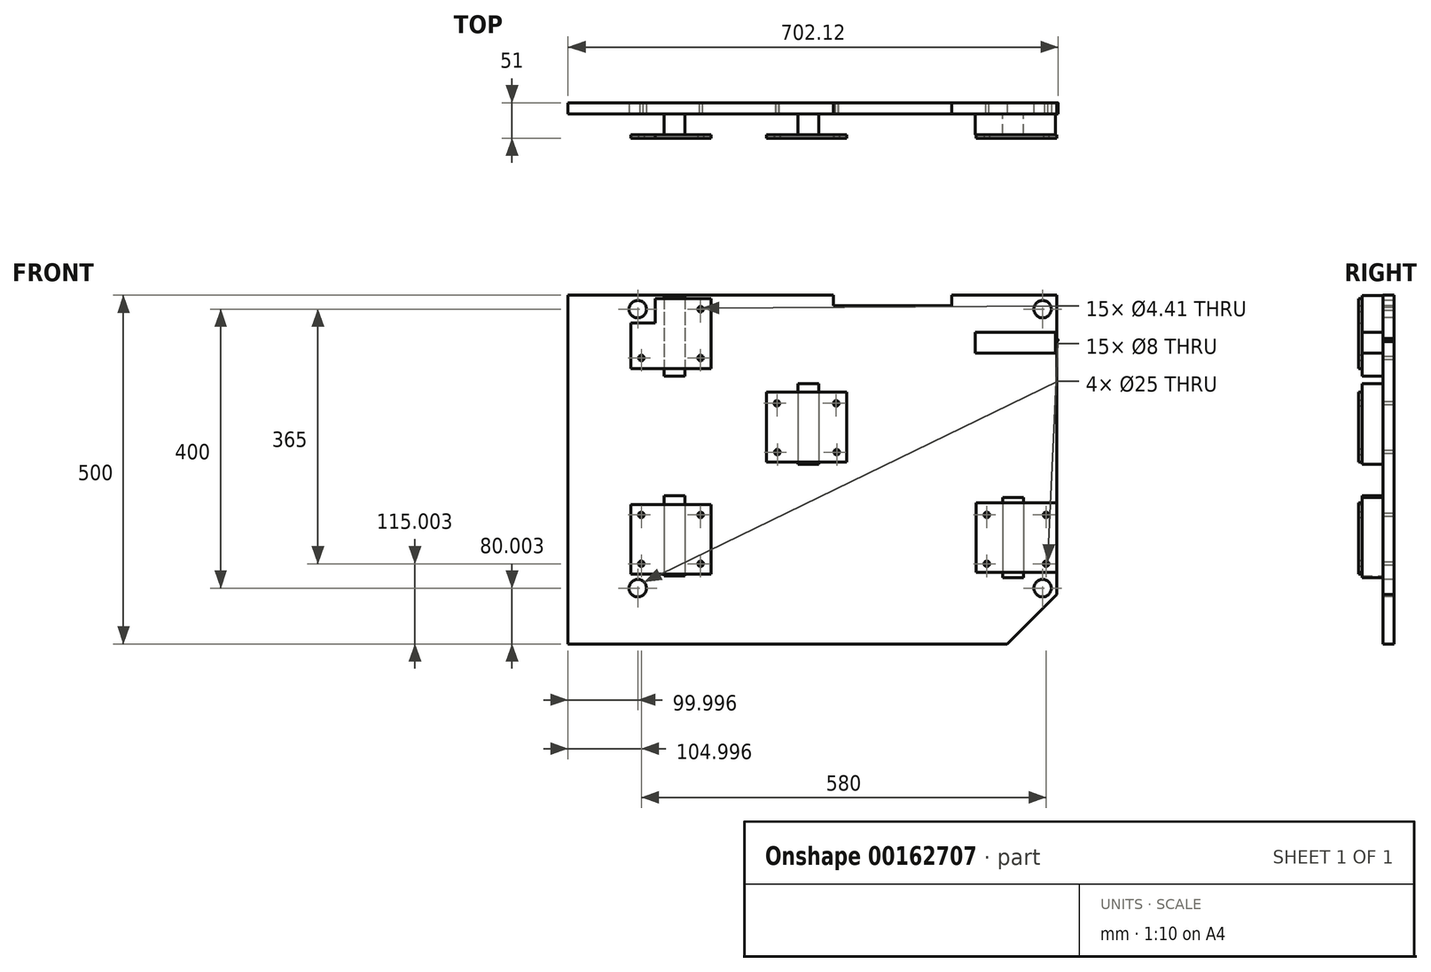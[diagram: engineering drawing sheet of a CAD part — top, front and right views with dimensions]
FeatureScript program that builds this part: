
annotation { "Feature Type Name" : "Feature", "Feature Type Description" : "" }
export const myFeature = defineFeature(function(context is Context, id is Id, definition is map)
    precondition{}
    {
        {
            var Q0;
            Q0=qCreatedBy(makeId("Front.planeOp"),FACE);
            var sketch = newSketch(context, id + "F0", { "sketchPlane" : qUnion([Q0])});
            skLineSegment(sketch, "E0", {"start": v(-699.91, -435.58) * mm, "end": v(-699.91, 64.42) * mm});
            skLineSegment(sketch, "E1", {"start": v(-699.91, 64.42) * mm, "end": v(-319.91, 64.42) * mm});
            skLineSegment(sketch, "E2", {"start": v(-319.91, 64.42) * mm, "end": v(-319.91, 49.42) * mm});
            skLineSegment(sketch, "E3", {"start": v(-319.91, 49.42) * mm, "end": v(-149.91, 49.42) * mm});
            skLineSegment(sketch, "E4", {"start": v(-149.91, 49.42) * mm, "end": v(-149.91, 64.42) * mm});
            skLineSegment(sketch, "E5", {"start": v(-149.91, 64.42) * mm, "end": v(0.09, 64.42) * mm});
            skLineSegment(sketch, "E6", {"start": v(0.09, 64.42) * mm, "end": v(0.09, -364.91) * mm});
            skLineSegment(sketch, "E7", {"start": v(38.78, -125.58) * mm, "end": v(-754.12, -125.58) * mm, "construction": true});
            skLineSegment(sketch, "E8", {"start": v(-70.58, -435.58) * mm, "end": v(-699.91, -435.58) * mm});
            skPoint(sketch, "E9.visualSharp", {"position": v(0.09, -435.58) * mm});
            skLineSegment(sketch, "E10", {"start": v(0.09, -364.91) * mm, "end": v(-70.58, -435.58) * mm});
            skCircle(sketch, "E11", {"center": v(-19.91, 44.42) * mm, "radius": 12.5 * mm});
            skCircle(sketch, "E12", {"center": v(-19.91, -355.58) * mm, "radius": 12.5 * mm});
            skCircle(sketch, "E13", {"center": v(-599.91, -355.58) * mm, "radius": 12.5 * mm});
            skCircle(sketch, "E14", {"center": v(-399.91, -160.58) * mm, "radius": 2.2 * mm});
            skCircle(sketch, "E15", {"center": v(-400.63, -90.58) * mm, "radius": 2.2 * mm});
            skCircle(sketch, "E16", {"center": v(-315.63, -90.58) * mm, "radius": 2.2 * mm});
            skCircle(sketch, "E17", {"center": v(-314.91, -160.58) * mm, "radius": 2.2 * mm});
            skCircle(sketch, "E18", {"center": v(0, 0) * mm, "radius": 2.2 * mm});
            skCircle(sketch, "E19", {"center": v(-594.91, -25.58) * mm, "radius": 2.2 * mm});
            skCircle(sketch, "E20", {"center": v(-594.91, 44.42) * mm, "radius": 2.2 * mm});
            skCircle(sketch, "E21", {"center": v(-509.91, 44.42) * mm, "radius": 2.2 * mm});
            skCircle(sketch, "E22", {"center": v(-509.91, -25.58) * mm, "radius": 2.2 * mm});
            skCircle(sketch, "E23", {"center": v(-594.91, -320.58) * mm, "radius": 2.2 * mm});
            skCircle(sketch, "E24", {"center": v(-594.91, -250.58) * mm, "radius": 2.2 * mm});
            skCircle(sketch, "E25", {"center": v(-509.91, -250.58) * mm, "radius": 2.2 * mm});
            skCircle(sketch, "E26", {"center": v(-509.91, -320.58) * mm, "radius": 2.2 * mm});
            skCircle(sketch, "E27", {"center": v(-99.91, -320.58) * mm, "radius": 2.2 * mm});
            skCircle(sketch, "E28", {"center": v(-99.91, -250.58) * mm, "radius": 2.2 * mm});
            skCircle(sketch, "E29", {"center": v(-14.91, -250.58) * mm, "radius": 2.2 * mm});
            skCircle(sketch, "E30", {"center": v(-14.91, -320.58) * mm, "radius": 2.2 * mm});
            skCircle(sketch, "E31", {"center": v(-599.91, 44.42) * mm, "radius": 12.5 * mm});
            skSolve(sketch);
        }
        {
            var Q0;
            Q0=qSketchRegion(id+"F0",true);
            extrude(context, id + "F1", {"entities" : qUnion([Q0]), "oppositeDirection" : true, "depth" : 16 * mm});
        }
        {
            var Q0;
            Q0=qCreatedBy(makeId("Front.planeOp"),FACE);
            var sketch = newSketch(context, id + "F2", { "sketchPlane" : qUnion([Q0])});
            skLineSegment(sketch, "E32.bottom", {"start": v(-562.12, -222.78) * mm, "end": v(-532.12, -222.78) * mm});
            skLineSegment(sketch, "E32.top", {"start": v(-562.12, -337.78) * mm, "end": v(-532.12, -337.78) * mm});
            skLineSegment(sketch, "E32.left", {"start": v(-562.12, -222.78) * mm, "end": v(-562.12, -337.78) * mm});
            skLineSegment(sketch, "E32.right", {"start": v(-532.12, -222.78) * mm, "end": v(-532.12, -337.78) * mm});
            skLineSegment(sketch, "E33.bottom", {"start": v(-370.68, -62.7) * mm, "end": v(-340.68, -62.7) * mm});
            skLineSegment(sketch, "E33.top", {"start": v(-370.68, -177.7) * mm, "end": v(-340.68, -177.7) * mm});
            skLineSegment(sketch, "E33.left", {"start": v(-370.68, -62.7) * mm, "end": v(-370.68, -177.7) * mm});
            skLineSegment(sketch, "E33.right", {"start": v(-340.68, -62.7) * mm, "end": v(-340.68, -177.7) * mm});
            skLineSegment(sketch, "E34.bottom", {"start": v(-562.2, 63.72) * mm, "end": v(-532.2, 63.72) * mm});
            skLineSegment(sketch, "E34.top", {"start": v(-562.2, -51.28) * mm, "end": v(-532.2, -51.28) * mm});
            skLineSegment(sketch, "E34.left", {"start": v(-562.2, 63.72) * mm, "end": v(-562.2, -51.28) * mm});
            skLineSegment(sketch, "E34.right", {"start": v(-532.2, 63.72) * mm, "end": v(-532.2, -51.28) * mm});
            skLineSegment(sketch, "E35.bottom", {"start": v(-77.3, -225.43) * mm, "end": v(-47.3, -225.43) * mm});
            skLineSegment(sketch, "E35.top", {"start": v(-77.3, -340.43) * mm, "end": v(-47.3, -340.43) * mm});
            skLineSegment(sketch, "E35.left", {"start": v(-77.3, -225.43) * mm, "end": v(-77.3, -340.43) * mm});
            skLineSegment(sketch, "E35.right", {"start": v(-47.3, -225.43) * mm, "end": v(-47.3, -340.43) * mm});
            skLineSegment(sketch, "E36.bottom", {"start": v(-1.77, 11.17) * mm, "end": v(-1.77, -18.83) * mm});
            skLineSegment(sketch, "E36.top", {"start": v(-116.77, 11.17) * mm, "end": v(-116.77, -18.83) * mm});
            skLineSegment(sketch, "E36.left", {"start": v(-1.77, 11.17) * mm, "end": v(-116.77, 11.17) * mm});
            skLineSegment(sketch, "E36.right", {"start": v(-1.77, -18.83) * mm, "end": v(-116.77, -18.83) * mm});
            skSolve(sketch);
        }
        {
            var Q0;
            Q0=qSketchRegion(id+"F2",true);
            extrude(context, id + "F3", {"entities" : qUnion([Q0]), "operationType" : NewBodyOperationType.ADD, "depth" : 30 * mm});
        }
        {
            var Q0;
            Q0=makeQuery(id+"F3.opExtrude","CAP_FACE",FACE,{"disambiguationData":[OSD([sQuery(id+"F2.wireOp",EDGE,"E32.bottom"),sQuery(id+"F2.wireOp",EDGE,"E32.top"),sQuery(id+"F2.wireOp",EDGE,"E32.left"),sQuery(id+"F2.wireOp",EDGE,"E32.right")])],"isStart":false});
            var sketch = newSketch(context, id + "F4", { "sketchPlane" : qUnion([Q0])});
            skLineSegment(sketch, "E37.top", {"start": v(279.66, -576.3) * mm, "end": v(-947.78, -576.3) * mm});
            skLineSegment(sketch, "E37.right", {"start": v(-947.78, 301.05) * mm, "end": v(-947.78, -576.3) * mm});
            skLineSegment(sketch, "E38.bottom", {"start": v(-562.12, -337.78) * mm, "end": v(-532.12, -337.78) * mm});
            skLineSegment(sketch, "E38.top", {"start": v(-562.12, -222.78) * mm, "end": v(-532.12, -222.78) * mm});
            skLineSegment(sketch, "E38.left", {"start": v(-562.12, -337.78) * mm, "end": v(-562.12, -222.78) * mm});
            skLineSegment(sketch, "E38.right", {"start": v(-532.12, -337.78) * mm, "end": v(-532.12, -222.78) * mm});
            skSolve(sketch);
        }
        {
            var Q0;
            Q0=makeQuery(id+"F4.imprint","IMPRINT",FACE,{"disambiguationData":[TD([[makeQuery(id+"F4.imprint","IMPRINT",EDGE,{"derivedFrom":sQuery(id+"F4.wireOp",EDGE,"E38.bottom")}),1.0]])]});
            var sketch = newSketch(context, id + "F5", { "sketchPlane" : qUnion([Q0])});
            skLineSegment(sketch, "E39", {"start": v(-494.91, -235.58) * mm, "end": v(-609.91, -235.58) * mm});
            skLineSegment(sketch, "E40", {"start": v(-609.91, -235.58) * mm, "end": v(-609.91, -335.58) * mm});
            skLineSegment(sketch, "E41", {"start": v(-609.91, -335.58) * mm, "end": v(-494.91, -335.58) * mm});
            skLineSegment(sketch, "E42", {"start": v(-494.91, -335.58) * mm, "end": v(-494.91, -235.58) * mm});
            skSolve(sketch);
        }
        {
            var Q0;
            {var subQ0=sQuery(id+"F5.wireOp",EDGE,"E40");Q0=makeQuery(id+"F5.imprint","IMPRINT",FACE,{"disambiguationData":[TD([[makeQuery(id+"F5.imprint","IMPRINT",EDGE,{"derivedFrom":subQ0}),1.0]])]});}
            var Q1;
            {var subQ0=sQuery(id+"F5.wireOp",EDGE,"E39");var subQ1=makeQuery(id+"F4.imprint","IMPRINT",EDGE,{"derivedFrom":sQuery(id+"F4.wireOp",EDGE,"E38.right")});var subQ2=makeQuery(id+"F5.imprint","INTERSECT",VERTEX,{"derivedFrom":[subQ1,subQ0]});Q1=makeQuery(id+"F5.imprint","IMPRINT",FACE,{"disambiguationData":[TD([[makeQuery(id+"F5.imprint","IMPRINT",EDGE,{"disambiguationData":[TD([[subQ2,-1.0]])],"derivedFrom":subQ0}),1.0]])]});}
            var Q2;
            {var subQ0=sQuery(id+"F5.wireOp",EDGE,"E42");Q2=makeQuery(id+"F5.imprint","IMPRINT",FACE,{"disambiguationData":[TD([[makeQuery(id+"F5.imprint","IMPRINT",EDGE,{"derivedFrom":subQ0}),1.0]])]});}
            extrude(context, id + "F6", {"entities" : qUnion([Q0, Q1, Q2]), "operationType" : NewBodyOperationType.ADD, "depth" : 5 * mm});
        }
        {
            var Q0;
            Q0=makeQuery(id+"F3.opExtrude","CAP_FACE",FACE,{"disambiguationData":[OSD([sQuery(id+"F2.wireOp",EDGE,"E35.bottom"),sQuery(id+"F2.wireOp",EDGE,"E35.top"),sQuery(id+"F2.wireOp",EDGE,"E35.left"),sQuery(id+"F2.wireOp",EDGE,"E35.right")])],"isStart":false});
            var sketch = newSketch(context, id + "F7", { "sketchPlane" : qUnion([Q0])});
            skLineSegment(sketch, "E43", {"start": v(0.09, -232.93) * mm, "end": v(-114.91, -232.93) * mm});
            skLineSegment(sketch, "E44", {"start": v(-114.91, -232.93) * mm, "end": v(-114.91, -332.93) * mm});
            skLineSegment(sketch, "E45", {"start": v(-114.91, -332.93) * mm, "end": v(0.09, -332.93) * mm});
            skLineSegment(sketch, "E46", {"start": v(0.09, -332.93) * mm, "end": v(0.09, -232.93) * mm});
            skSolve(sketch);
        }
        {
            var Q0;
            Q0=qSketchRegion(id+"F7",true);
            extrude(context, id + "F8", {"entities" : qUnion([Q0]), "operationType" : NewBodyOperationType.ADD, "depth" : 5 * mm});
        }
        {
            var Q0;
            Q0=makeQuery(id+"F3.opExtrude","CAP_FACE",FACE,{"disambiguationData":[OSD([sQuery(id+"F2.wireOp",EDGE,"E34.bottom"),sQuery(id+"F2.wireOp",EDGE,"E34.top"),sQuery(id+"F2.wireOp",EDGE,"E34.left"),sQuery(id+"F2.wireOp",EDGE,"E34.right")])],"isStart":false});
            var sketch = newSketch(context, id + "F9", { "sketchPlane" : qUnion([Q0])});
            skLineSegment(sketch, "E47", {"start": v(-494.91, 59.42) * mm, "end": v(-574.91, 59.42) * mm});
            skLineSegment(sketch, "E48", {"start": v(-609.91, 24.42) * mm, "end": v(-609.91, -40.58) * mm});
            skLineSegment(sketch, "E49", {"start": v(-609.91, -40.58) * mm, "end": v(-494.91, -40.58) * mm});
            skLineSegment(sketch, "E50", {"start": v(-494.91, -40.58) * mm, "end": v(-494.91, 59.42) * mm});
            skLineSegment(sketch, "E51", {"start": v(-574.91, 59.42) * mm, "end": v(-574.91, 24.42) * mm});
            skLineSegment(sketch, "E52", {"start": v(-574.91, 24.42) * mm, "end": v(-609.91, 24.42) * mm});
            skSolve(sketch);
        }
        {
            var Q0;
            Q0=makeQuery(id+"F3.opExtrude","CAP_FACE",FACE,{"disambiguationData":[OSD([sQuery(id+"F2.wireOp",EDGE,"E33.bottom"),sQuery(id+"F2.wireOp",EDGE,"E33.top"),sQuery(id+"F2.wireOp",EDGE,"E33.left"),sQuery(id+"F2.wireOp",EDGE,"E33.right")])],"isStart":false});
            var sketch = newSketch(context, id + "F10", { "sketchPlane" : qUnion([Q0])});
            skLineSegment(sketch, "E53", {"start": v(-300.63, -74.7) * mm, "end": v(-415.63, -74.7) * mm});
            skLineSegment(sketch, "E54", {"start": v(-415.63, -74.7) * mm, "end": v(-415.63, -174.7) * mm});
            skLineSegment(sketch, "E55", {"start": v(-415.63, -174.7) * mm, "end": v(-300.63, -174.7) * mm});
            skLineSegment(sketch, "E56", {"start": v(-300.63, -174.7) * mm, "end": v(-300.63, -74.7) * mm});
            skSolve(sketch);
        }
        {
            var Q0;
            Q0=qSketchRegion(id+"F10",true);
            extrude(context, id + "F11", {"entities" : qUnion([Q0]), "operationType" : NewBodyOperationType.ADD, "depth" : 5 * mm});
        }
        {
            var Q0;
            Q0=makeQuery(id+"F0.imprint","IMPRINT",FACE,{"disambiguationData":[TD([[makeQuery(id+"F0.imprint","IMPRINT",EDGE,{"derivedFrom":sQuery(id+"F0.wireOp",EDGE,"E0")}),-1.0]])]});
            cPlane(context, id + "F12", {"entities" : qUnion([Q0]), "cplaneType" : CPlaneType.OFFSET, "offset" : 30 * mm, "width" : 150 * mm, "height" : 150 * mm});
        }
        {
            var Q0;
            {var subQ5=sQuery(id+"F9.wireOp",EDGE,"E48");Q0=makeQuery(id+"F9.imprint","IMPRINT",FACE,{"disambiguationData":[TD([[makeQuery(id+"F9.imprint","IMPRINT",EDGE,{"derivedFrom":subQ5}),1.0]])]});}
            var Q1;
            {var subQ0=sQuery(id+"F9.wireOp",EDGE,"E47");var subQ1=makeQuery(id+"F3.opExtrude","CAP_EDGE",EDGE,{"disambiguationData":[OSD([sQuery(id+"F2.wireOp",EDGE,"E34.right")])],"isStart":false});var subQ2=makeQuery(id+"F9.imprint","INTERSECT",VERTEX,{"derivedFrom":[subQ1,subQ0]});Q1=makeQuery(id+"F9.imprint","IMPRINT",FACE,{"disambiguationData":[TD([[makeQuery(id+"F9.imprint","IMPRINT",EDGE,{"disambiguationData":[TD([[subQ2,-1.0]])],"derivedFrom":subQ0}),1.0]])]});}
            var Q2;
            {var subQ0=sQuery(id+"F9.wireOp",EDGE,"E50");Q2=makeQuery(id+"F9.imprint","IMPRINT",FACE,{"disambiguationData":[TD([[makeQuery(id+"F9.imprint","IMPRINT",EDGE,{"derivedFrom":subQ0}),1.0]])]});}
            extrude(context, id + "F13", {"entities" : qUnion([Q0, Q1, Q2]), "operationType" : NewBodyOperationType.ADD, "depth" : 5 * mm});
        }
        {
            var Q0;
            Q0=sQuery(id+"F0.wireOp",VERTEX,"E24.center");
            var Q1;
            Q1=sQuery(id+"F0.wireOp",VERTEX,"E23.center");
            var Q2;
            Q2=sQuery(id+"F0.wireOp",VERTEX,"E26.center");
            var Q3;
            Q3=sQuery(id+"F0.wireOp",VERTEX,"E25.center");
            var Q4;
            Q4=sQuery(id+"F0.wireOp",VERTEX,"E15.center");
            var Q5;
            Q5=sQuery(id+"F0.wireOp",VERTEX,"E16.center");
            var Q6;
            Q6=sQuery(id+"F0.wireOp",VERTEX,"E14.center");
            var Q7;
            Q7=sQuery(id+"F0.wireOp",VERTEX,"E17.center");
            var Q8;
            Q8=sQuery(id+"F0.wireOp",VERTEX,"E19.center");
            var Q9;
            Q9=sQuery(id+"F0.wireOp",VERTEX,"E22.center");
            var Q10;
            Q10=sQuery(id+"F0.wireOp",VERTEX,"E21.center");
            var Q11;
            Q11=sQuery(id+"F0.wireOp",VERTEX,"E27.center");
            var Q12;
            Q12=sQuery(id+"F0.wireOp",VERTEX,"E28.center");
            var Q13;
            Q13=sQuery(id+"F0.wireOp",VERTEX,"E30.center");
            var Q14;
            Q14=sQuery(id+"F0.wireOp",VERTEX,"E29.center");
            var Q15;
            Q15=makeQuery(id+"F1.opExtrude","SWEPT_BODY",BODY,{"disambiguationData":[OSD([sQuery(id+"F0.wireOp",EDGE,"E0"),sQuery(id+"F0.wireOp",EDGE,"E1"),sQuery(id+"F0.wireOp",EDGE,"E2"),sQuery(id+"F0.wireOp",EDGE,"E3"),sQuery(id+"F0.wireOp",EDGE,"E4"),sQuery(id+"F0.wireOp",EDGE,"E5"),sQuery(id+"F0.wireOp",EDGE,"E6"),sQuery(id+"F0.wireOp",EDGE,"E8"),sQuery(id+"F0.wireOp",EDGE,"E10"),sQuery(id+"F0.wireOp",EDGE,"E11"),sQuery(id+"F0.wireOp",EDGE,"E12"),sQuery(id+"F0.wireOp",EDGE,"E13"),sQuery(id+"F0.wireOp",EDGE,"E14"),sQuery(id+"F0.wireOp",EDGE,"E15"),sQuery(id+"F0.wireOp",EDGE,"E16"),sQuery(id+"F0.wireOp",EDGE,"E17"),sQuery(id+"F0.wireOp",EDGE,"E18"),sQuery(id+"F0.wireOp",EDGE,"E19"),sQuery(id+"F0.wireOp",EDGE,"E21"),sQuery(id+"F0.wireOp",EDGE,"E22"),sQuery(id+"F0.wireOp",EDGE,"E23"),sQuery(id+"F0.wireOp",EDGE,"E24"),sQuery(id+"F0.wireOp",EDGE,"E25"),sQuery(id+"F0.wireOp",EDGE,"E26"),sQuery(id+"F0.wireOp",EDGE,"E27"),sQuery(id+"F0.wireOp",EDGE,"E28"),sQuery(id+"F0.wireOp",EDGE,"E29"),sQuery(id+"F0.wireOp",EDGE,"E30"),sQuery(id+"F0.wireOp",EDGE,"E31")])]});
            hole(context, id + "F14", {"style" : HoleStyle.SIMPLE, "endStyle" : HoleEndStyle.THROUGH, "oppositeDirection" : true, "holeDiameter" : 8 * mm, "locations" : qUnion([Q0, Q1, Q2, Q3, Q4, Q5, Q6, Q7, Q8, Q9, Q10, Q11, Q12, Q13, Q14]), "scope" : qUnion([Q15]), "isTappedThrough" : true});
        }
    });
